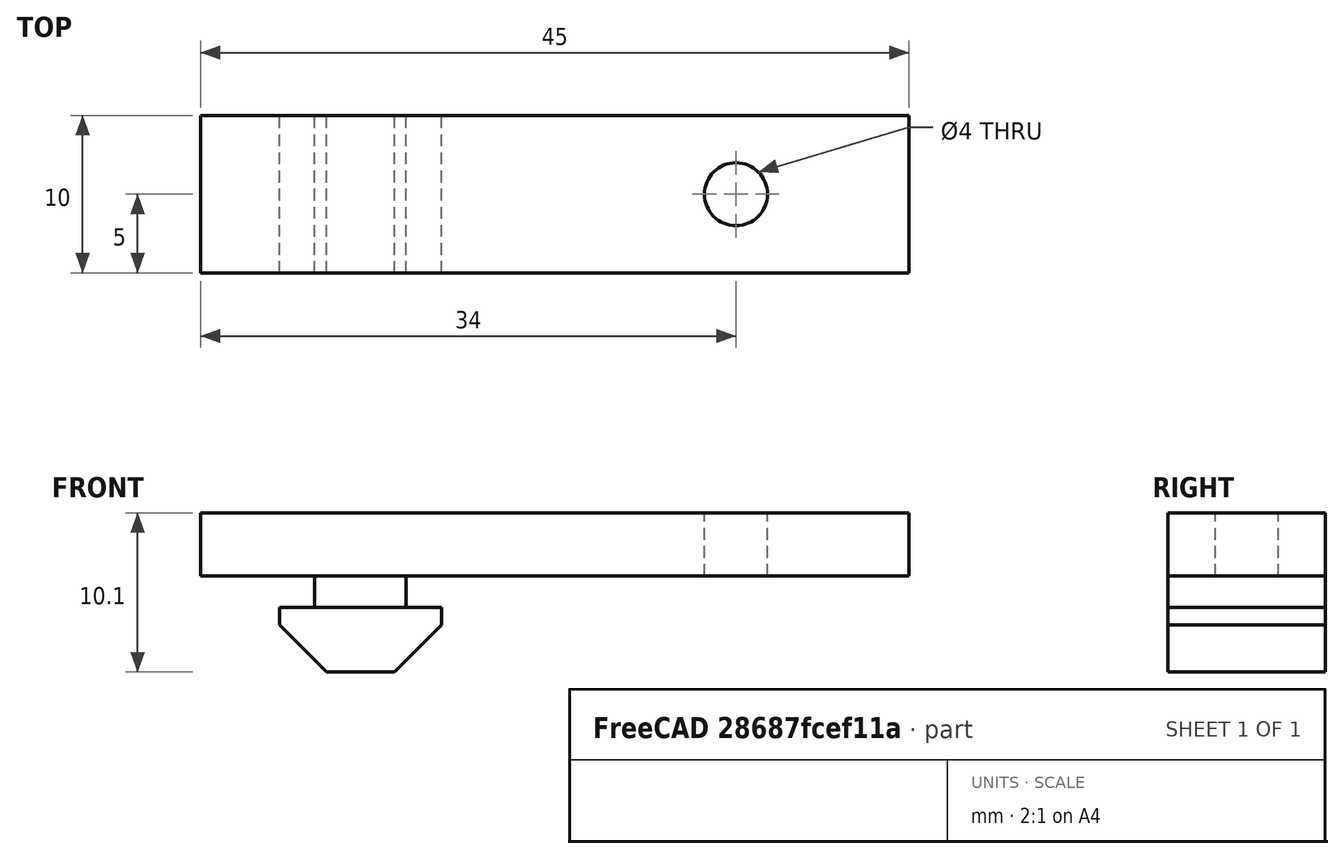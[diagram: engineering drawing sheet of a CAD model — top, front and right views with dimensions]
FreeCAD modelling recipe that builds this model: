
FCSTD DOCUMENT  (FreeCAD 0.18.4R)
Label: nuts
License: All rights reserved
LicenseURL: http://en.wikipedia.org/wiki/All_rights_reserved
objects: Part::Box×3, Part::Chamfer×2, Part::Cylinder×1, Part::Cut×1
note: 7 computed .brp shape members not serialized (recipe doc carries the construction recipe); baked Part::Feature solids carry a one-line shape summary decoded from their .brp

FEATURE [Part::Box] Box  label="Cube"
  AttacherType = Attacher::AttachEngine3D
  Height = 4.1
  Length = 10.3
  Width = 10
FEATURE [Part::Box] Box001  label="Cube001"
  AttacherType = Attacher::AttachEngine3D
  Height = 2
  Length = 5.8
  Placement = pos=(2.25,0,4.1) rot=(0,0,1;0rad)
  Width = 10
FEATURE [Part::Chamfer] Chamfer
  Base = -> Box
  Edges = 1 edges r=3: [Edge4]
FEATURE [Part::Chamfer] Chamfer001
  Base = -> Chamfer
  Edges = 1 edges r=3: [Edge15]
FEATURE [Part::Box] Box002  label="Cube002"
  AttacherType = Attacher::AttachEngine3D
  Height = 4
  Length = 45
  Placement = pos=(-5,0,6.1) rot=(0,0,1;0rad)
  Width = 10
FEATURE [Part::Cylinder] Cylinder
  Angle = 360
  AttacherType = Attacher::AttachEngine3D
  Height = 10
  Placement = pos=(29,5,1) rot=(0,0,1;0rad)
  Radius = 2
FEATURE [Part::Cut] Cut
  Base = -> Box002
  Tool = -> Cylinder
